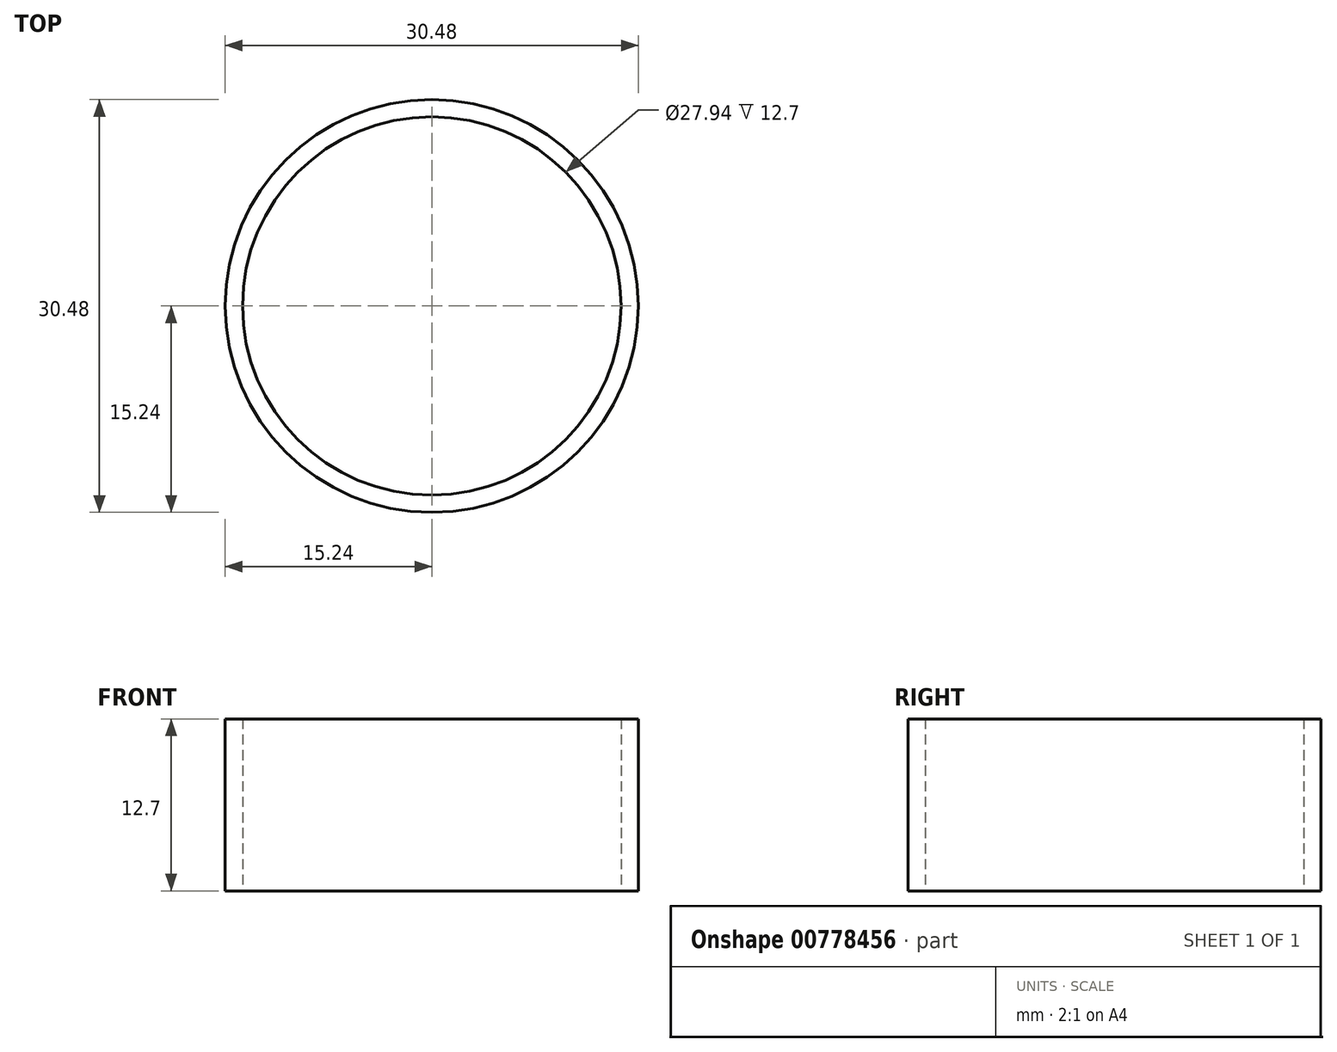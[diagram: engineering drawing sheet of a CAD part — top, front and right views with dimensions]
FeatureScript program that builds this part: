
annotation { "Feature Type Name" : "Feature", "Feature Type Description" : "" }
export const myFeature = defineFeature(function(context is Context, id is Id, definition is map)
    precondition{}
    {
        {
            var Q0;
            Q0=qCreatedBy(makeId("Top.planeOp"),FACE);
            var sketch = newSketch(context, id + "F0", { "sketchPlane" : qUnion([Q0])});
            skCircle(sketch, "E0", {"center": v(0, 0) * mm, "radius": 15.24 * mm});
            skSolve(sketch);
        }
        {
            var Q0;
            Q0 = qSketchRegion(id + "F0", true);
            extrude(context, id + "F1", {"entities" : qUnion([Q0]), "depth" : 12.7 * mm, "offsetDistance" : 25.4 * mm});
        }
        {
            var Q0;
            Q0=qCreatedBy(makeId("Top.planeOp"),FACE);
            var sketch = newSketch(context, id + "F2", { "sketchPlane" : qUnion([Q0])});
            skCircle(sketch, "E1", {"center": v(-10.6, 18.63) * mm, "radius": 13.97 * mm});
            skSolve(sketch);
        }
        {
            var Q0;
            Q0 = qSketchRegion(id + "F2", true);
            extrude(context, id + "F3", {"entities" : qUnion([Q0]), "operationType" : NewBodyOperationType.REMOVE, "oppositeDirection" : true, "depth" : 12.7 * mm, "offsetDistance" : 25.4 * mm});
        }
        {
            var Q0;
            Q0=qCreatedBy(makeId("Top.planeOp"),FACE);
            var sketch = newSketch(context, id + "F4", { "sketchPlane" : qUnion([Q0])});
            skCircle(sketch, "E2", {"center": v(0, 0) * mm, "radius": 13.97 * mm});
            skSolve(sketch);
        }
        {
            var Q0;
            Q0 = qSketchRegion(id + "F4", true);
            extrude(context, id + "F5", {"entities" : qUnion([Q0]), "operationType" : NewBodyOperationType.REMOVE, "depth" : 12.7 * mm, "offsetDistance" : 25.4 * mm});
        }
    });
